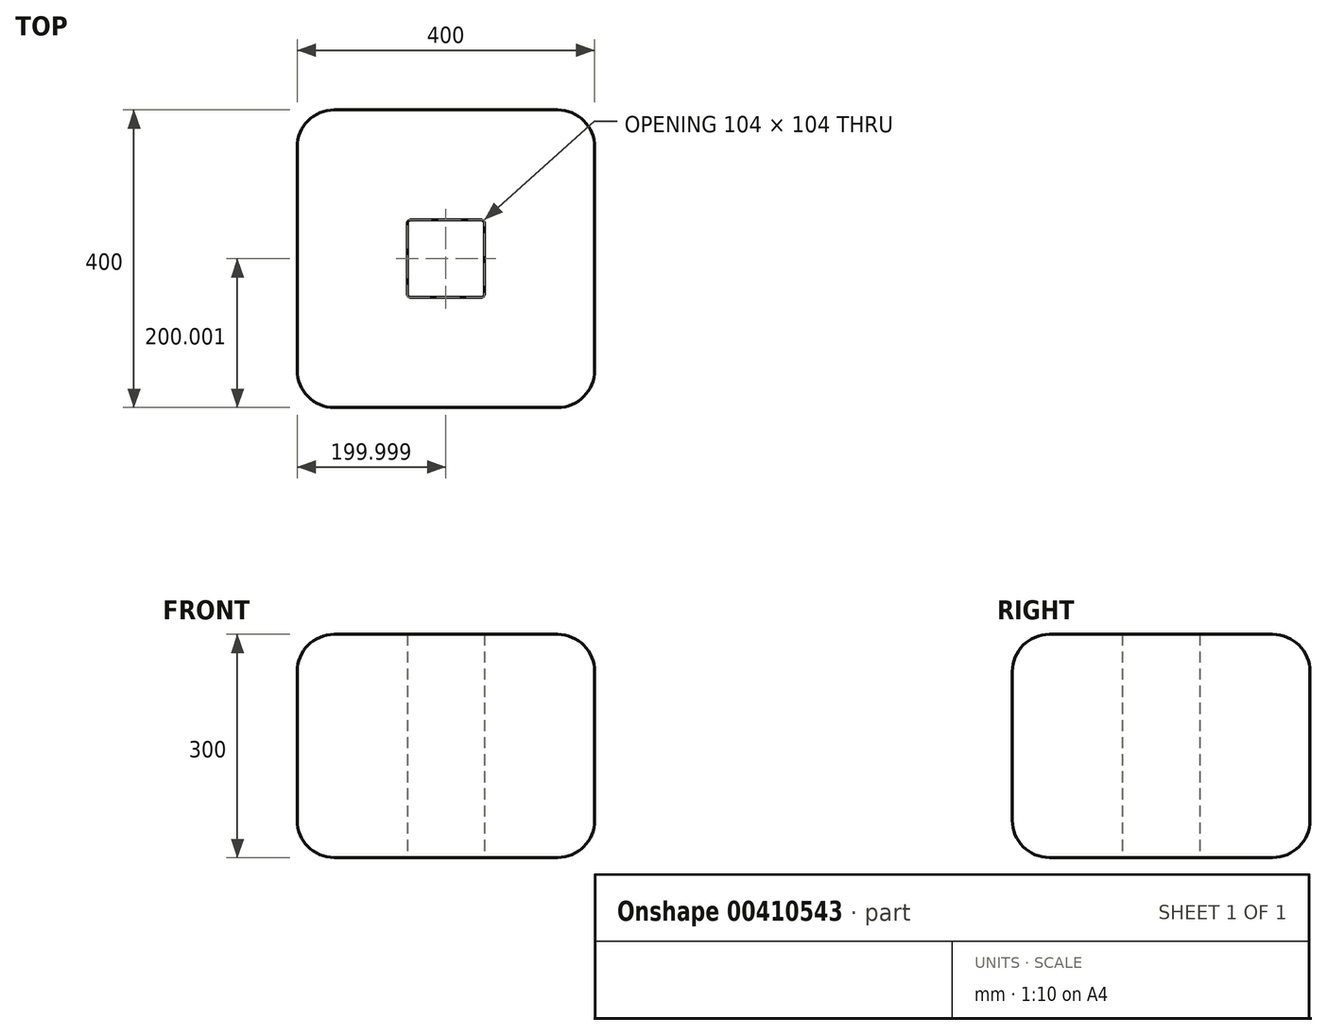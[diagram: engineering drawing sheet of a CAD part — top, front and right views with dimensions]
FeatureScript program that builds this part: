
annotation { "Feature Type Name" : "Feature", "Feature Type Description" : "" }
export const myFeature = defineFeature(function(context is Context, id is Id, definition is map)
    precondition{}
    {
        {
            var Q0;
            Q0=qCreatedBy(makeId("Top.planeOp"),FACE);
            var sketch = newSketch(context, id + "F0", { "sketchPlane" : qUnion([Q0])});
            skLineSegment(sketch, "E0.bottom", {"start": v(225.85, 118.97) * mm, "end": v(-174.15, 118.97) * mm});
            skLineSegment(sketch, "E0.top", {"start": v(225.85, -281.03) * mm, "end": v(-174.15, -281.03) * mm});
            skLineSegment(sketch, "E0.left", {"start": v(225.85, 118.97) * mm, "end": v(225.85, -281.03) * mm});
            skLineSegment(sketch, "E0.right", {"start": v(-174.15, 118.97) * mm, "end": v(-174.15, -281.03) * mm});
            skLineSegment(sketch, "E1.bottom", {"start": v(77.85, -29.03) * mm, "end": v(-26.15, -29.03) * mm});
            skLineSegment(sketch, "E1.top", {"start": v(77.85, -133.03) * mm, "end": v(-26.15, -133.03) * mm});
            skLineSegment(sketch, "E1.left", {"start": v(77.85, -29.03) * mm, "end": v(77.85, -133.03) * mm});
            skLineSegment(sketch, "E1.right", {"start": v(-26.15, -29.03) * mm, "end": v(-26.15, -133.03) * mm});
            skSolve(sketch);
        }
        {
            var Q0;
            Q0=makeQuery(id+"F0.imprint","IMPRINT",FACE,{"disambiguationData":[TD([[makeQuery(id+"F0.imprint","IMPRINT",EDGE,{"derivedFrom":sQuery(id+"F0.wireOp",EDGE,"E0.bottom")}),1.0]])]});
            extrude(context, id + "F1", {"entities" : qUnion([Q0]), "depth" : 300 * mm});
        }
        {
            var Q0;
            Q0=makeQuery(id+"F1.opExtrude","SWEPT_FACE",FACE,{"disambiguationData":[OSD([sQuery(id+"F0.wireOp",EDGE,"E0.top")])]});
            var Q1;
            Q1=makeQuery(id+"F1.opExtrude","SWEPT_FACE",FACE,{"disambiguationData":[OSD([sQuery(id+"F0.wireOp",EDGE,"E0.left")])]});
            var Q2;
            Q2=makeQuery(id+"F1.opExtrude","SWEPT_FACE",FACE,{"disambiguationData":[OSD([sQuery(id+"F0.wireOp",EDGE,"E0.bottom")])]});
            var Q3;
            Q3=makeQuery(id+"F1.opExtrude","SWEPT_FACE",FACE,{"disambiguationData":[OSD([sQuery(id+"F0.wireOp",EDGE,"E0.right")])]});
            fillet(context, id + "F2", {"entities" : qUnion([Q0, Q1, Q2, Q3]), "radius" : 50 * mm, "tangentPropagation" : true, "allowEdgeOverflow" : false});
        }
        {
            var Q0;
            Q0=makeQuery(id+"F1.opExtrude","SWEPT_EDGE",EDGE,{"disambiguationData":[OSD([sQuery(id+"F0.wireOp",EDGE,"E1.bottom"),sQuery(id+"F0.wireOp",EDGE,"E1.right")])]});
            var Q1;
            Q1=makeQuery(id+"F1.opExtrude","SWEPT_EDGE",EDGE,{"disambiguationData":[OSD([sQuery(id+"F0.wireOp",EDGE,"E1.bottom"),sQuery(id+"F0.wireOp",EDGE,"E1.left")])]});
            var Q2;
            Q2=makeQuery(id+"F1.opExtrude","SWEPT_EDGE",EDGE,{"disambiguationData":[OSD([sQuery(id+"F0.wireOp",EDGE,"E1.top"),sQuery(id+"F0.wireOp",EDGE,"E1.left")])]});
            var Q3;
            Q3=makeQuery(id+"F1.opExtrude","SWEPT_EDGE",EDGE,{"disambiguationData":[OSD([sQuery(id+"F0.wireOp",EDGE,"E1.top"),sQuery(id+"F0.wireOp",EDGE,"E1.right")])]});
            fillet(context, id + "F3", {"entities" : qUnion([Q0, Q1, Q2, Q3]), "radius" : 5 * mm, "tangentPropagation" : true, "allowEdgeOverflow" : false});
        }
    });
